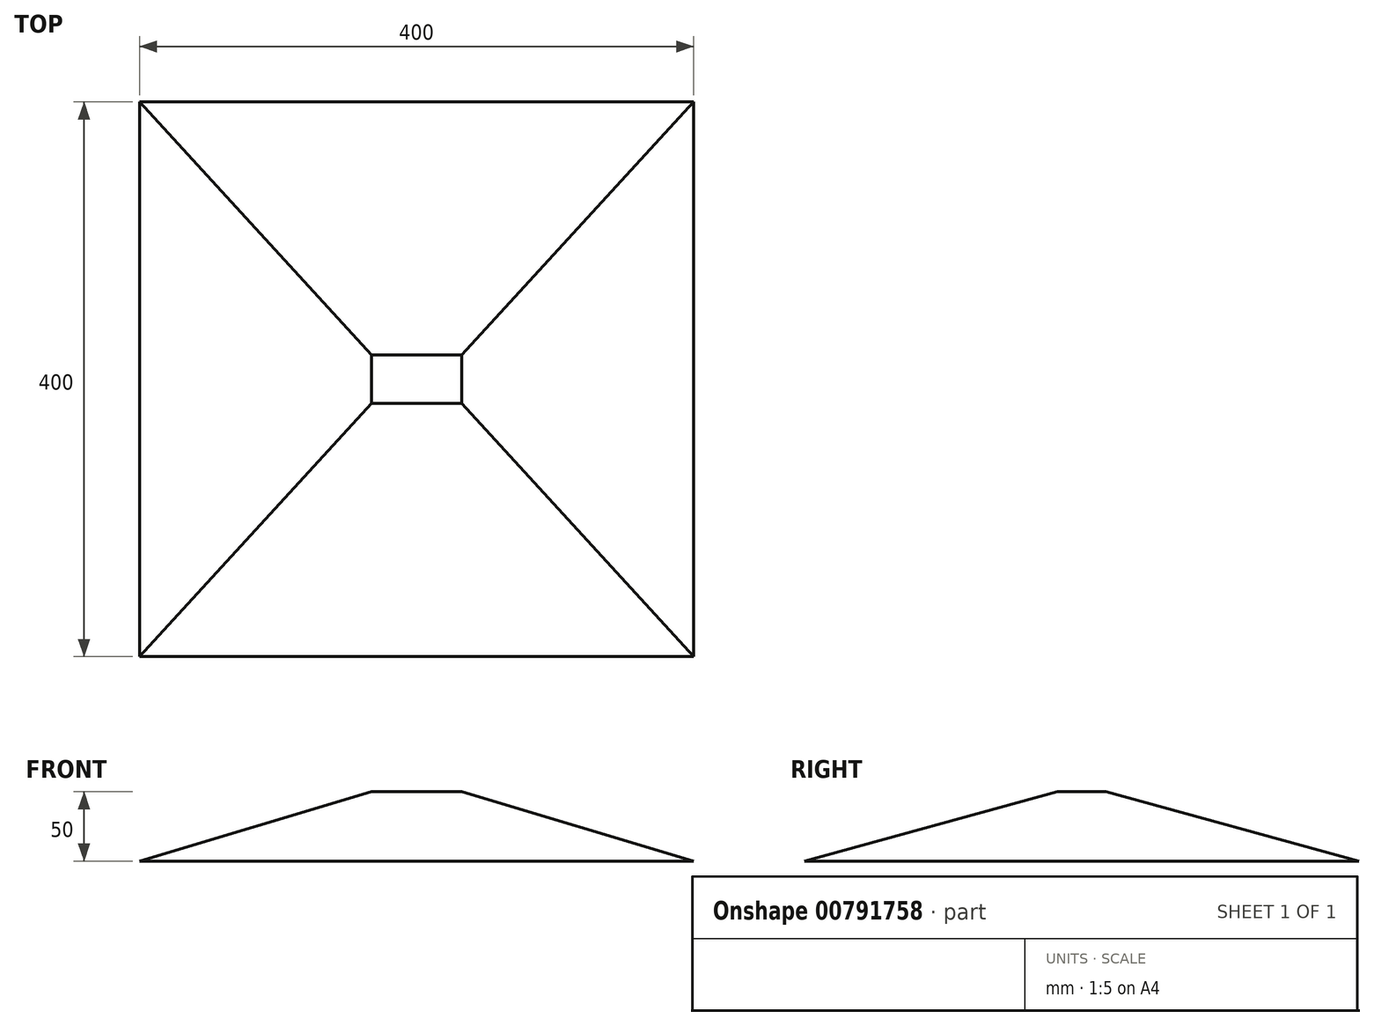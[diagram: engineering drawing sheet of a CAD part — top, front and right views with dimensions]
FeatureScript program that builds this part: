
annotation { "Feature Type Name" : "Feature", "Feature Type Description" : "" }
export const myFeature = defineFeature(function(context is Context, id is Id, definition is map)
    precondition{}
    {
        {
            var Q0;
            Q0=qCreatedBy(makeId("Top.planeOp"),FACE);
            var sketch = newSketch(context, id + "F0", { "sketchPlane" : qUnion([Q0])});
            skLineSegment(sketch, "E0.bottom", {"start": v(200, 200) * mm, "end": v(-200, 200) * mm});
            skLineSegment(sketch, "E0.top", {"start": v(200, -200) * mm, "end": v(-200, -200) * mm});
            skLineSegment(sketch, "E0.left", {"start": v(200, 200) * mm, "end": v(200, -200) * mm});
            skLineSegment(sketch, "E0.right", {"start": v(-200, 200) * mm, "end": v(-200, -200) * mm});
            skPoint(sketch, "E0.middle", {"position": v(0, 0) * mm});
            skSolve(sketch);
        }
        {
            var Q0;
            Q0=makeQuery(id+"F0.imprint","IMPRINT",FACE,{"disambiguationData":[TD([[makeQuery(id+"F0.imprint","IMPRINT",EDGE,{"derivedFrom":sQuery(id+"F0.wireOp",EDGE,"E0.bottom")}),1.0]])]});
            cPlane(context, id + "F1", {"entities" : qUnion([Q0]), "cplaneType" : CPlaneType.OFFSET, "offset" : 50 * mm, "width" : 150 * mm, "height" : 150 * mm});
        }
        {
            var Q0;
            Q0=qCreatedBy(id+"F1.planeOp",FACE);
            var sketch = newSketch(context, id + "F2", { "sketchPlane" : qUnion([Q0])});
            skLineSegment(sketch, "E1.bottom", {"start": v(-32.5, 17.5) * mm, "end": v(32.5, 17.5) * mm});
            skLineSegment(sketch, "E1.top", {"start": v(-32.5, -17.5) * mm, "end": v(32.5, -17.5) * mm});
            skLineSegment(sketch, "E1.left", {"start": v(-32.5, 17.5) * mm, "end": v(-32.5, -17.5) * mm});
            skLineSegment(sketch, "E1.right", {"start": v(32.5, 17.5) * mm, "end": v(32.5, -17.5) * mm});
            skPoint(sketch, "E1.middle", {"position": v(0, 0) * mm});
            skSolve(sketch);
        }
        {
            var Q0;
            Q0=makeQuery(id+"F0.imprint","IMPRINT",FACE,{"disambiguationData":[TD([[makeQuery(id+"F0.imprint","IMPRINT",EDGE,{"derivedFrom":sQuery(id+"F0.wireOp",EDGE,"E0.bottom")}),1.0]])]});
            var Q1;
            Q1=makeQuery(id+"F2.imprint","IMPRINT",FACE,{"disambiguationData":[TD([[makeQuery(id+"F2.imprint","IMPRINT",EDGE,{"derivedFrom":sQuery(id+"F2.wireOp",EDGE,"E1.bottom")}),-1.0]])]});
            loft(context, id + "F3", {"sheetProfilesArray" : [{ "sheetProfileEntities" : qUnion([Q0]) }, { "sheetProfileEntities" : qUnion([Q1]) }]});
        }
    });
